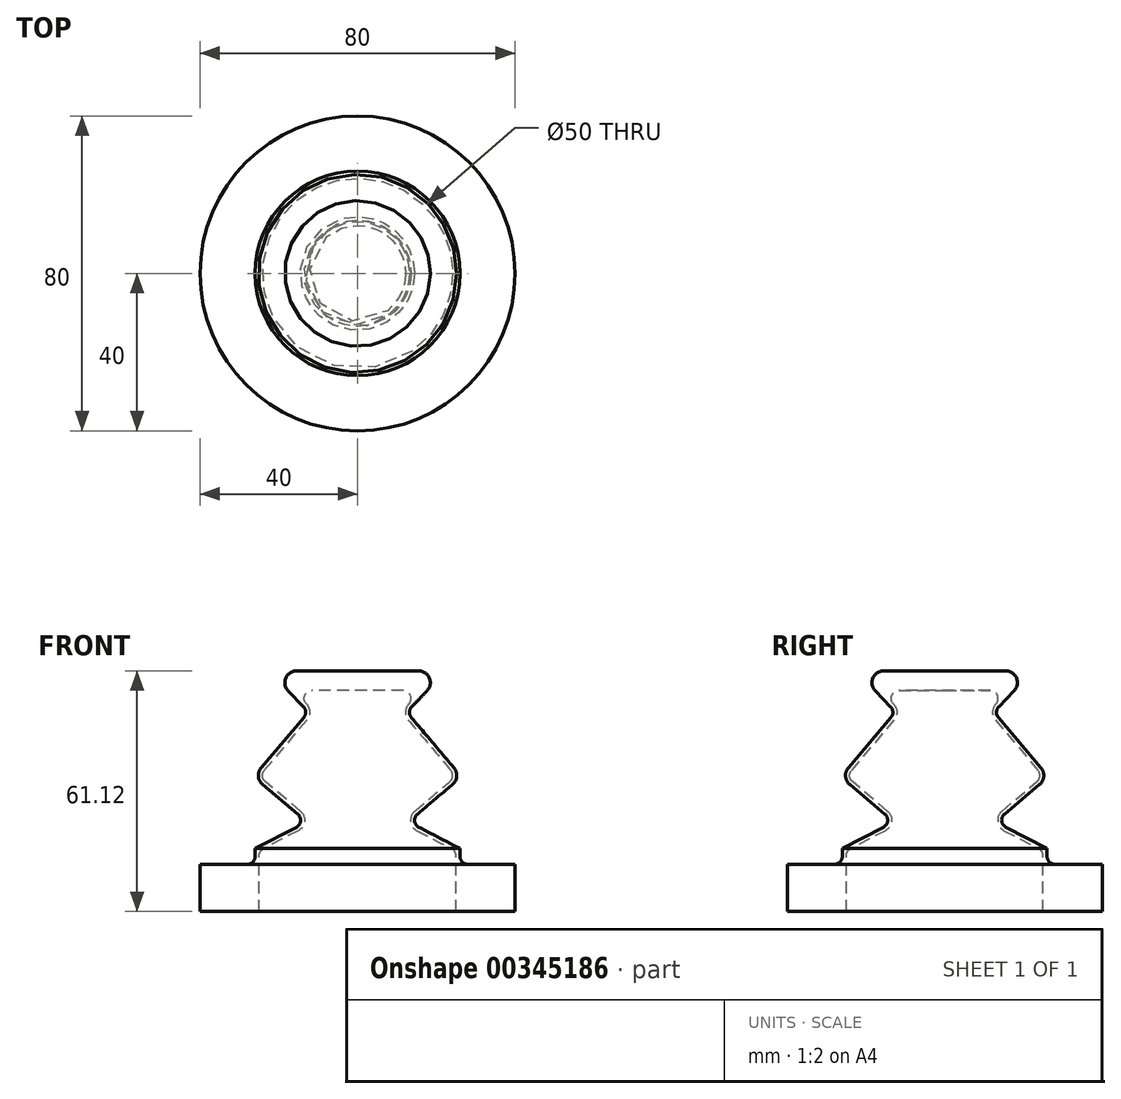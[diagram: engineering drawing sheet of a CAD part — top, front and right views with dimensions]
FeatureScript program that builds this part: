
annotation { "Feature Type Name" : "Feature", "Feature Type Description" : "" }
export const myFeature = defineFeature(function(context is Context, id is Id, definition is map)
    precondition{}
    {
        {
            var Q0;
            Q0=qCreatedBy(makeId("Front.planeOp"),FACE);
            var sketch = newSketch(context, id + "F0", { "sketchPlane" : qUnion([Q0])});
            skLineSegment(sketch, "E0", {"start": v(0, 63.93) * mm, "end": v(0, -55.51) * mm, "construction": true});
            skLineSegment(sketch, "E1", {"start": v(-40, 0) * mm, "end": v(-40, 12) * mm});
            skLineSegment(sketch, "E2", {"start": v(-28, 12) * mm, "end": v(-40, 12) * mm});
            skLineSegment(sketch, "E3", {"start": v(-26, 14) * mm, "end": v(-26, 16) * mm});
            skLineSegment(sketch, "E4", {"start": v(-40, 0) * mm, "end": v(-25, 0) * mm});
            skLineSegment(sketch, "E5", {"start": v(-25, 0) * mm, "end": v(-25, 14.18) * mm});
            skLineSegment(sketch, "E6", {"start": v(-23.92, 15.95) * mm, "end": v(-15.09, 20.54) * mm});
            skLineSegment(sketch, "E7", {"start": v(-14.54, 25.5) * mm, "end": v(-23.47, 33.04) * mm});
            skLineSegment(sketch, "E8", {"start": v(-23.7, 35.86) * mm, "end": v(-12.87, 48.7) * mm});
            skLineSegment(sketch, "E9", {"start": v(-10.8, 50.45) * mm, "end": v(-13.01, 52.73) * mm});
            skLineSegment(sketch, "E10.0", {"start": v(-8.77, 46.94) * mm, "end": v(-13.73, 52.03) * mm});
            skLineSegment(sketch, "E10.1", {"start": v(-24.47, 36.5) * mm, "end": v(-13.63, 49.34) * mm});
            skLineSegment(sketch, "E10.2", {"start": v(-15.18, 24.73) * mm, "end": v(-24.12, 32.28) * mm});
            skLineSegment(sketch, "E10.3", {"start": v(-26, 16) * mm, "end": v(-15.55, 21.43) * mm});
            skPoint(sketch, "E11.orphan", {"position": v(-26, 15.4) * mm});
            skPoint(sketch, "E12.visualSharp", {"position": v(-25, 34.34) * mm});
            skArc(sketch, "E12.filletArc", {"start": v(-23.7, 35.86) * mm, "mid": v(-24.17, 34.4) * mm, "end": v(-23.47, 33.04) * mm});
            skPoint(sketch, "E13.visualSharp", {"position": v(-12.46, 50.73) * mm});
            skArc(sketch, "E13.filletArc", {"start": v(-13.63, 49.34) * mm, "mid": v(-13.16, 50.7) * mm, "end": v(-13.73, 52.03) * mm});
            skPoint(sketch, "E14.visualSharp", {"position": v(-12.9, 22.8) * mm});
            skArc(sketch, "E14.filletArc", {"start": v(-15.55, 21.43) * mm, "mid": v(-14.48, 22.98) * mm, "end": v(-15.18, 24.73) * mm});
            skPoint(sketch, "E15.visualSharp", {"position": v(-26, 12) * mm});
            skArc(sketch, "E15.filletArc", {"start": v(-28, 12) * mm, "mid": v(-26.59, 12.59) * mm, "end": v(-26, 14) * mm});
            skPoint(sketch, "E16.visualSharp", {"position": v(-25, 15.4) * mm});
            skArc(sketch, "E16.filletArc", {"start": v(-23.92, 15.95) * mm, "mid": v(-24.7, 15.22) * mm, "end": v(-25, 14.18) * mm});
            skPoint(sketch, "E17.visualSharp", {"position": v(-26.4, 34.22) * mm});
            skArc(sketch, "E17.filletArc", {"start": v(-24.47, 36.5) * mm, "mid": v(-25.17, 34.32) * mm, "end": v(-24.12, 32.28) * mm});
            skPoint(sketch, "E18.visualSharp", {"position": v(-11.11, 22.6) * mm});
            skArc(sketch, "E18.filletArc", {"start": v(-15.09, 20.54) * mm, "mid": v(-13.49, 22.87) * mm, "end": v(-14.54, 25.5) * mm});
            skPoint(sketch, "E19.visualSharp", {"position": v(-11.11, 50.78) * mm});
            skArc(sketch, "E19.filletArc", {"start": v(-12.87, 48.7) * mm, "mid": v(-12.16, 50.74) * mm, "end": v(-13.01, 52.73) * mm});
            skLineSegment(sketch, "E20", {"start": v(-11.58, 56.12) * mm, "end": v(0, 56.12) * mm});
            skLineSegment(sketch, "E21", {"start": v(-8.77, 46.94) * mm, "end": v(-17.63, 56.03) * mm});
            skLineSegment(sketch, "E22", {"start": v(-15.48, 61.12) * mm, "end": v(0, 61.12) * mm});
            skPoint(sketch, "E23.visualSharp", {"position": v(-16.33, 56.12) * mm});
            skArc(sketch, "E23.filletArc", {"start": v(-11.58, 56.12) * mm, "mid": v(-13.43, 54.9) * mm, "end": v(-13.01, 52.73) * mm});
            skPoint(sketch, "E24.visualSharp", {"position": v(-22.6, 61.12) * mm});
            skArc(sketch, "E24.filletArc", {"start": v(-15.48, 61.12) * mm, "mid": v(-18.25, 59.29) * mm, "end": v(-17.63, 56.03) * mm});
            skPoint(sketch, "E25.visualSharp", {"position": v(-10.84, 49.06) * mm});
            skLineSegment(sketch, "E25.filletArc", {"start": v(-8.77, 46.94) * mm, "end": v(-8.77, 46.94) * mm});
            skPoint(sketch, "E26.visualSharp", {"position": v(-25, 65.02) * mm});
            skLineSegment(sketch, "E26.filletArc", {"start": v(-10.8, 50.45) * mm, "end": v(-10.8, 50.45) * mm});
            skLineSegment(sketch, "E27", {"start": v(0, 56.12) * mm, "end": v(0, 61.12) * mm});
            skSolve(sketch);
        }
        {
            var Q0;
            Q0 = qSketchRegion(id + "F0", true);
            var Q1;
            Q1=sQuery(id+"F0.wireOp",EDGE,"E0");
            revolve(context, id + "F1", {"entities" : qUnion([Q0]), "axis" : qUnion([Q1]), "revolveType" : RevolveType.FULL});
        }
    });
